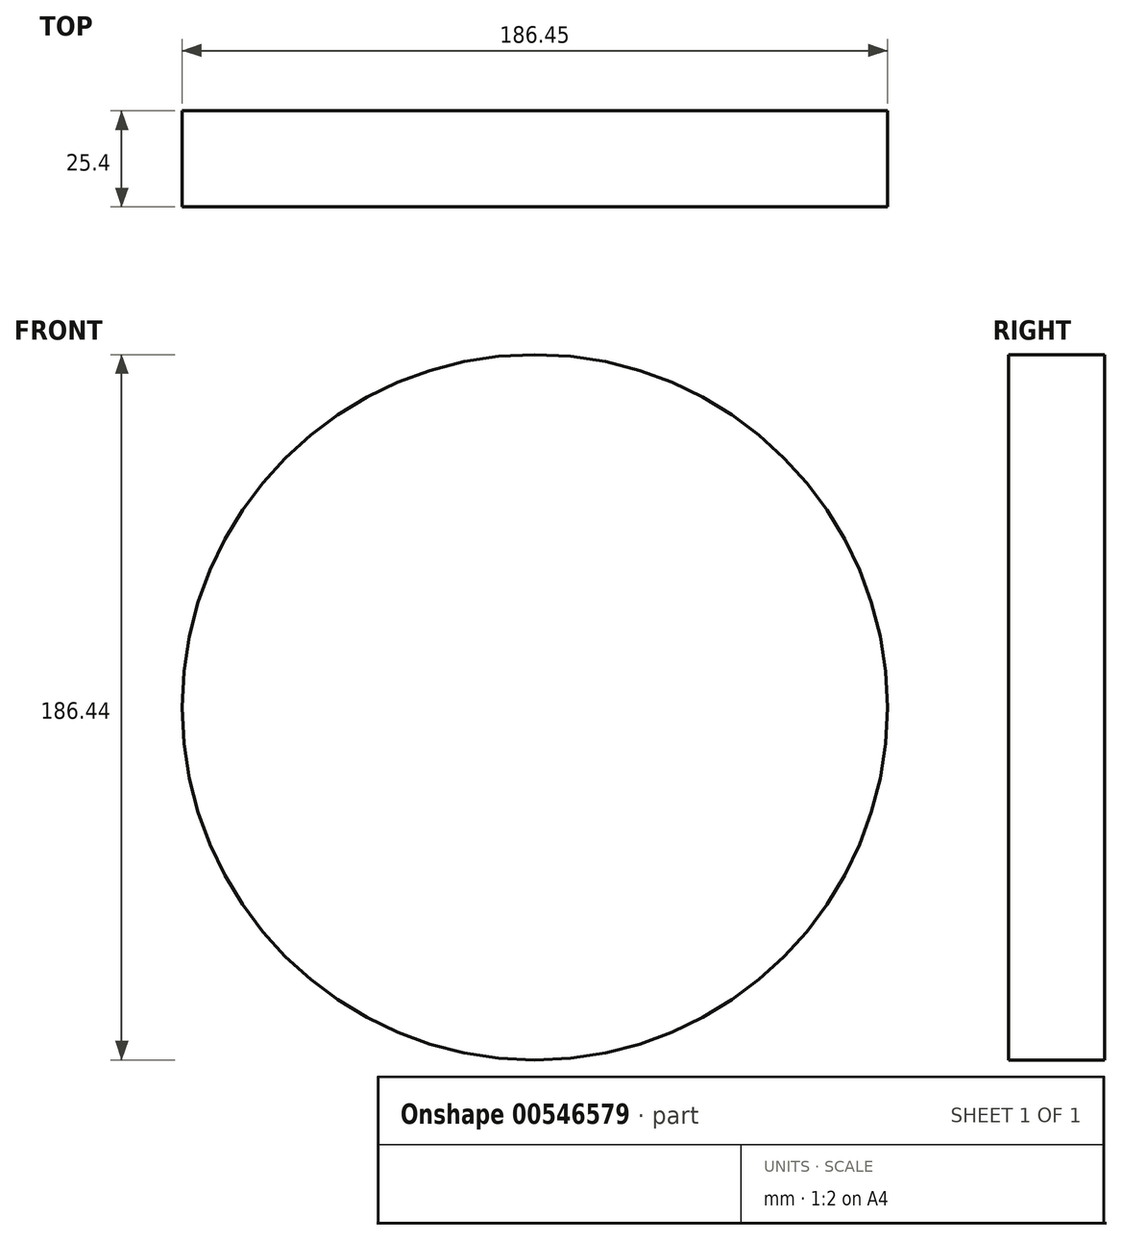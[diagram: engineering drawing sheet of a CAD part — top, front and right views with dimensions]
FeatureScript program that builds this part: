
annotation { "Feature Type Name" : "Feature", "Feature Type Description" : "" }
export const myFeature = defineFeature(function(context is Context, id is Id, definition is map)
    precondition{}
    {
        {
            var Q0;
            Q0=qCreatedBy(makeId("Front.planeOp"),FACE);
            var sketch = newSketch(context, id + "F0", { "sketchPlane" : qUnion([Q0])});
            skCircle(sketch, "E0", {"center": v(-110.38, 45.49) * mm, "radius": 93.22 * mm});
            skSolve(sketch);
        }
        {
            var Q0;
            Q0 = qSketchRegion(id + "F0", true);
            extrude(context, id + "F1", {"entities" : qUnion([Q0]), "depth" : 25.4 * mm, "offsetDistance" : 25.4 * mm});
        }
    });
